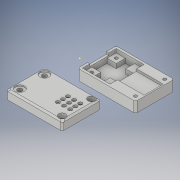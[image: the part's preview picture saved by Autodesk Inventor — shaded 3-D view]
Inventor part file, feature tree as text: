
AUTODESK INVENTOR PART (.ipt)
format: ipt  version: 2019 (Build 230136000, 136)  size: 1,405,440 bytes
history: native  units: mm
features: move_body x28, sketch x26, extrude x24, direct_edit x18, chamfer x4, delete_face x2, split x1
ambient origin geometry x8: Origin, YZ Plane, XZ Plane, XY Plane, X Axis, Y Axis, Z Axis, Center Point
bodies: Solid1 (feature_tree), Solid2 (feature_tree), Solid3 (feature_tree)
feature tree (103):
  sketch  "Sketch1"  dims[d0=21.0mm d1=25.0mm]
  sketch  "Sketch2"  dims[d2=5.0mm d3=0.0mm d4=14.5mm]
  extrude  "Extrusion1"  Depth=25.0mm
  extrude  "Extrusion2"  Depth=14.5mm
  extrude  "Extrusion3"  Depth=1.5mm
  extrude  "Extrusion4"  Depth=6.0mm
  extrude  "Extrusion5"  Depth=6.0mm
  extrude  "Extrusion6"  Depth=6.0mm
  direct_edit  "Direct Edit1"
  extrude  "Extrusion7"  Depth=6.0mm
  direct_edit  "Direct Edit2"
  extrude  "Extrusion8"  Depth=6.0mm
  extrude  "Extrusion9"  Depth=6.0mm
  direct_edit  "Direct Edit3"
  extrude  "Extrusion10"  Depth=6.0mm
  extrude  "Extrusion11"  Depth=6.0mm
  sketch  "Sketch12"  dims[d26=6.0mm d27=1.1mm d28=0.0mm]
  direct_edit  "Direct Edit4"
  extrude  "Extrusion12"  Depth=1.1mm TaperAngle=0.0deg
  sketch  "Sketch14"  dims[d31=2.0mm d32=2.0mm]
  direct_edit  "Direct Edit5"
  direct_edit  "Direct Edit6"
  direct_edit  "Direct Edit7"
  direct_edit  "Direct Edit8"
  direct_edit  "Direct Edit9"
  sketch  "Sketch15"  dims[d33=2.0mm d34=0.0mm d35=1.0mm]
  direct_edit  "Direct Edit10"
  extrude  "Extrusion13"  Depth=2.0mm
  extrude  "Extrusion14"  Depth=2.0mm
  extrude  "Extrusion15"  Depth=1.0mm
  extrude  "Extrusion16"  Depth=1.0mm
  extrude  "Extrusion17"  Depth=1.0mm TaperAngle=0.0deg
  extrude  "Extrusion18"  Depth=0.5mm TaperAngle=0.0deg
  split  "Split1"
  chamfer  "Chamfer1"  Distance=1.0mm
  chamfer  "Chamfer2"  Distance=8.0mm
  extrude  "Extrusion19"  Depth=7.25mm
  delete_face  "Delete Face1"
  delete_face  "Delete Face2"
  direct_edit  "Direct Edit11"
  extrude  "Extrusion20"  Depth=6.0mm
  direct_edit  "Direct Edit12"
  direct_edit  "Direct Edit13"
  sketch  "Sketch23"  dims[d58=16.5mm d59=0.0mm d60=0.0mm d61=0.0mm d62=0.5mm]
  sketch  "Sketch24"  dims[d63=2.0mm d64=16.5mm d65=0.0mm]
  direct_edit  "Direct Edit14"
  direct_edit  "Direct Edit15"
  extrude  "Extrusion21"  Depth=0.5mm TaperAngle=0.0deg
  direct_edit  "Direct Edit16"
  extrude  "Extrusion22"  Depth=2.0mm TaperAngle=0.0deg
  extrude  "Extrusion23"  TaperAngle=0.0deg  [1 undecoded]
  extrude  "Extrusion24"  Depth=2.0mm
  direct_edit  "Direct Edit17"
  direct_edit  "Direct Edit18"
  chamfer  "Chamfer3"  Distance=5.0mm
  chamfer  "Chamfer4"  Distance=5.25mm
  sketch  "Sketch3"  dims[d5=16.5mm d6=0.0mm d8=1.5mm]
  sketch  "Sketch4"  dims[d9=6.0mm d10=6.0mm]
  sketch  "Sketch5"  dims[d11=6.0mm d12=6.0mm]
  sketch  "Sketch6"  dims[d13=6.0mm d14=6.0mm]
  sketch  "Sketch7"  dims[d15=6.0mm d16=6.0mm]
  sketch  "Sketch8"  dims[d17=4.0mm d18=0.0mm d19=6.0mm]
  sketch  "Sketch9"  dims[d20=6.0mm d21=6.0mm]
  sketch  "Sketch10"  dims[d22=6.0mm d23=6.0mm]
  sketch  "Sketch11"  dims[d24=6.0mm d25=6.0mm]
  sketch  "Sketch13"  dims[d29=2.0mm d30=2.0mm]
  sketch  "Sketch16"  dims[d36=1.0mm d37=1.0mm]
  sketch  "Sketch17"  dims[d38=1.0mm d39=1.0mm d40=0.0mm]
  sketch  "Sketch18"  dims[d41=0.0mm d42=0.0mm d43=0.5mm d45=0.5mm d46=0.0mm]
  sketch  "Sketch19"  dims[d47=25.0mm]
  sketch  "Sketch20"  dims[d48=21.0mm d49=0.0mm d50=0.0mm d51=1.0mm d52=8.0mm d53=0.0mm]
  sketch  "Sketch21"  dims[d54=2.0mm d55=7.25mm]
  sketch  "Sketch22"  dims[d56=14.5mm d57=6.0mm]
  sketch  "Sketch25"  dims[d68=5.0mm d69=0.0mm d70=0.0mm d71=0.0mm d72=-1.0mm]
  sketch  "Sketch26"  dims[d73=12.3mm d74=1.2mm d75=5.0mm d76=0.0mm d77=0.0mm d78=0.0mm d79=5.25mm d80=0.0mm d81=0.0mm d82=5.25mm d83=0.0mm d84=0.0mm d85=5.25mm d86=0.0mm d87=0.0mm d88=5.25mm d89=0.0mm d90=0.0mm d91=2.0mm d92=0.0mm d93=0.0mm d94=13.75mm d96=2.5mm d97=30.0mm d99=3.25mm d100=30.0mm d102=4.0mm d105=5.0mm d106=0.0mm d107=12.5mm d108=10.7mm d109=1.5mm d110=0.0mm d111=12.3mm d112=4.3mm d113=1.5mm d114=0.0mm d115=6.0mm d116=4.86mm d117=6.0mm d118=4.86mm d119=6.0mm d120=6.0mm d121=6.0mm d122=6.0mm d123=3.0mm d124=3.0mm d125=3.0mm d126=3.0mm d127=3.0mm d128=0.0mm d129=6.0mm d130=6.0mm d131=6.0mm d132=6.0mm d133=6.0mm d134=6.0mm d135=5.0mm d136=0.0mm d137=6.0mm d138=6.0mm d139=6.0mm d140=6.0mm d141=2.0mm d142=0.0mm d144=1.0mm d145=2.0mm d146=45.0deg d147=1.0mm d148=2.0mm d149=45.0deg d150=0.6mm d151=0.0mm d152=0.0mm d153=-0.5mm d154=0.0mm d155=0.0mm d156=0.0mm d157=1.5mm d158=0.0mm d159=0.0mm d160=1.5mm d161=8.0mm d162=0.0mm d163=0.0mm d164=0.0mm d165=-0.25mm d166=0.0mm d167=0.0mm d168=-0.25mm d169=0.0mm d170=0.0mm d171=0.25mm d172=0.0mm d173=0.0mm d174=0.25mm d175=6.0mm d176=6.0mm d177=6.0mm d178=6.0mm d179=6.0mm d180=6.0mm d181=6.0mm d182=6.0mm d183=0.0mm d184=0.0mm d185=0.25mm d186=0.0mm d187=0.0mm d188=0.25mm d189=0.0mm d190=0.0mm d191=0.4mm d192=3.0mm d193=3.0mm d194=8.0mm d195=0.0mm d196=0.0mm d197=0.0mm d198=1.0mm d199=0.0mm d200=0.0mm d201=-1.25mm d202=4.5mm d203=4.5mm d204=3.0mm d205=0.0mm d206=2.0mm d207=2.0mm d208=3.0mm d209=0.0mm d210=1.0mm d211=1.0mm d212=1.5mm d213=0.0mm d214=0.0mm d215=0.0mm d216=-0.5mm d217=0.0mm d218=0.0mm d219=-1.2mm d220=0.0mm d221=0.0mm d222=-1.2mm d223=0.0mm d224=0.0mm d225=0.3mm d226=0.0mm d227=0.0mm d228=-1.0mm d229=0.0mm d230=0.0mm d231=1.0mm d232=1.0mm d233=2.0mm d234=45.0deg d235=1.0mm d236=2.0mm d237=45.0deg]
  move_body  "Move1"
  move_body  "Move2"
  move_body  "Move3"
  move_body  "Move4"
  move_body  "Move5"
  move_body  "Move6"
  move_body  "Move7"
  move_body  "Move8"
  move_body  "Move9"
  move_body  "Move10"
  move_body  "Move11"
  move_body  "Move12"
  move_body  "Move13"
  move_body  "Move14"
  move_body  "Move15"
  move_body  "Move16"
  move_body  "Move17"
  move_body  "Move18"
  move_body  "Move19"
  move_body  "Move20"
  move_body  "Move21"
  move_body  "Move22"
  move_body  "Move23"
  move_body  "Move24"
  move_body  "Move25"
  move_body  "Move26"
  move_body  "Move27"
  move_body  "Move28"
note: 1 required parameter value undecoded (feature->parameter linkage not recoverable at this tier; creation-order binding heuristic only, values carry confidence <= 0.55)
